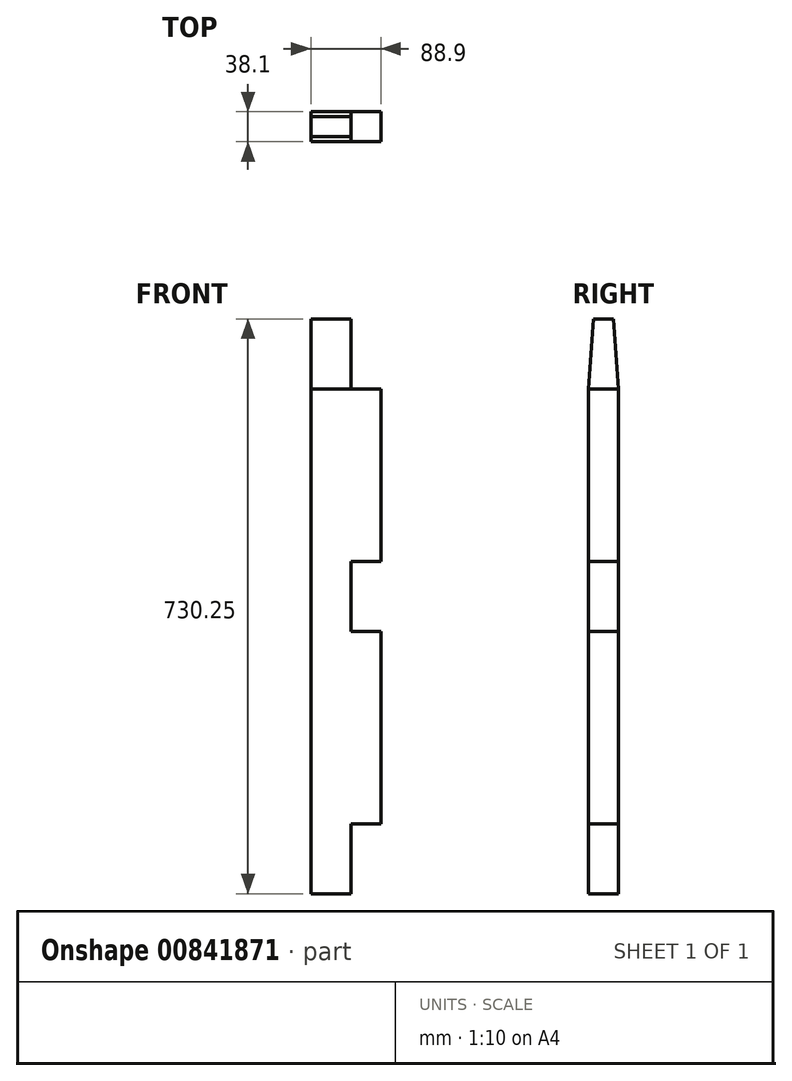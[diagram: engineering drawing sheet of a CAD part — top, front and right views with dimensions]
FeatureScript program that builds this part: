
annotation { "Feature Type Name" : "Feature", "Feature Type Description" : "" }
export const myFeature = defineFeature(function(context is Context, id is Id, definition is map)
    precondition{}
    {
        {
            var Q0;
            Q0=qCreatedBy(makeId("Top.planeOp"),FACE);
            var sketch = newSketch(context, id + "F0", { "sketchPlane" : qUnion([Q0])});
            skLineSegment(sketch, "E0.bottom", {"start": v(44.45, 19.05) * mm, "end": v(-44.45, 19.05) * mm});
            skLineSegment(sketch, "E0.top", {"start": v(44.45, -19.05) * mm, "end": v(-44.45, -19.05) * mm});
            skLineSegment(sketch, "E0.left", {"start": v(44.45, 19.05) * mm, "end": v(44.45, -19.05) * mm});
            skLineSegment(sketch, "E0.right", {"start": v(-44.45, 19.05) * mm, "end": v(-44.45, -19.05) * mm});
            skPoint(sketch, "E0.middle", {"position": v(0, 0) * mm});
            skSolve(sketch);
        }
        {
            var Q0;
            Q0 = qSketchRegion(id + "F0", true);
            extrude(context, id + "F1", {"entities" : qUnion([Q0]), "depth" : 730.25 * mm, "offsetDistance" : 25.4 * mm});
        }
        {
            var Q0;
            Q0=makeQuery(id+"F1.opExtrude","SWEPT_FACE",FACE,{"disambiguationData":[OSD([sQuery(id+"F0.wireOp",EDGE,"E0.top")])]});
            var sketch = newSketch(context, id + "F2", { "sketchPlane" : qUnion([Q0])});
            skLineSegment(sketch, "E1.bottom", {"start": v(44.45, 0) * mm, "end": v(6.35, 0) * mm});
            skLineSegment(sketch, "E1.top", {"start": v(44.45, 88.9) * mm, "end": v(6.35, 88.9) * mm});
            skLineSegment(sketch, "E1.left", {"start": v(44.45, 0) * mm, "end": v(44.45, 88.9) * mm});
            skLineSegment(sketch, "E1.right", {"start": v(6.35, 0) * mm, "end": v(6.35, 88.9) * mm});
            skLineSegment(sketch, "E2.bottom", {"start": v(44.45, 333.38) * mm, "end": v(6.35, 333.38) * mm});
            skLineSegment(sketch, "E2.top", {"start": v(44.45, 422.28) * mm, "end": v(6.35, 422.28) * mm});
            skLineSegment(sketch, "E2.left", {"start": v(44.45, 333.38) * mm, "end": v(44.45, 422.28) * mm});
            skLineSegment(sketch, "E2.right", {"start": v(6.35, 333.38) * mm, "end": v(6.35, 422.28) * mm});
            skLineSegment(sketch, "E3.bottom", {"start": v(44.45, 730.25) * mm, "end": v(6.35, 730.25) * mm});
            skLineSegment(sketch, "E3.top", {"start": v(44.45, 641.35) * mm, "end": v(6.35, 641.35) * mm});
            skLineSegment(sketch, "E3.left", {"start": v(44.45, 730.25) * mm, "end": v(44.45, 641.35) * mm});
            skLineSegment(sketch, "E3.right", {"start": v(6.35, 730.25) * mm, "end": v(6.35, 641.35) * mm});
            skSolve(sketch);
        }
        {
            var Q0;
            Q0 = qSketchRegion(id + "F2", true);
            extrude(context, id + "F3", {"entities" : qUnion([Q0]), "operationType" : NewBodyOperationType.REMOVE, "endBound" : BoundingType.THROUGH_ALL, "oppositeDirection" : true, "depth" : 25.4 * mm, "offsetDistance" : 25.4 * mm});
        }
        {
            var Q0;
            Q0=makeQuery(id+"F3.boolean.opBoolean","COPY",FACE,{"derivedFrom":makeQuery(id+"F3.opExtrude","SWEPT_FACE",FACE,{"disambiguationData":[OSD([sQuery(id+"F2.wireOp",EDGE,"E3.right")])]})});
            var sketch = newSketch(context, id + "F4", { "sketchPlane" : qUnion([Q0])});
            skLineSegment(sketch, "E4", {"start": v(-19.05, 730.25) * mm, "end": v(-19.05, 641.35) * mm});
            skLineSegment(sketch, "E5", {"start": v(-19.05, 641.35) * mm, "end": v(-12.7, 730.25) * mm});
            skLineSegment(sketch, "E6", {"start": v(-12.7, 730.25) * mm, "end": v(-19.05, 730.25) * mm});
            skLineSegment(sketch, "E7", {"start": v(19.05, 730.25) * mm, "end": v(19.05, 641.35) * mm});
            skLineSegment(sketch, "E8", {"start": v(19.05, 641.35) * mm, "end": v(12.7, 730.25) * mm});
            skLineSegment(sketch, "E9", {"start": v(12.7, 730.25) * mm, "end": v(19.05, 730.25) * mm});
            skSolve(sketch);
        }
        {
            var Q0;
            Q0 = qSketchRegion(id + "F4", true);
            extrude(context, id + "F5", {"entities" : qUnion([Q0]), "operationType" : NewBodyOperationType.REMOVE, "endBound" : BoundingType.THROUGH_ALL, "oppositeDirection" : true, "depth" : 25.4 * mm, "offsetDistance" : 25.4 * mm});
        }
    });
